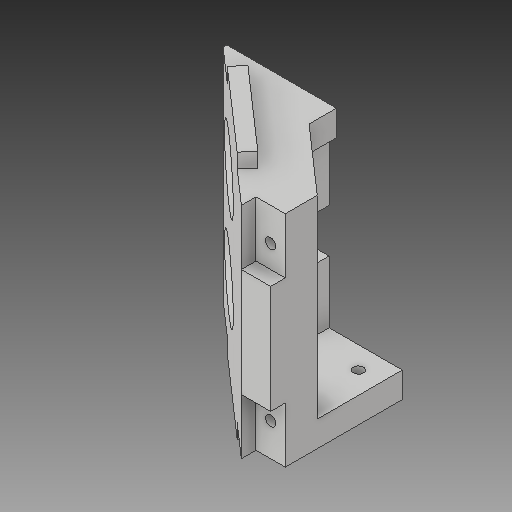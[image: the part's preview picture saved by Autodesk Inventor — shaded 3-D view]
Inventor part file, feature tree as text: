
AUTODESK INVENTOR PART (.ipt)
format: ipt  version: 2019 (Build 230136000, 136)  size: 202,752 bytes
history: native  units: mm
features: sketch x10, other x4, extrude x1, projected_geometry x1
ambient origin geometry x8: Origin, YZ Plane, XZ Plane, XY Plane, X Axis, Y Axis, Z Axis, Center Point
bodies: Body1 (feature_tree)
feature tree (16):
  other  "Sensor.ipt"
  extrude  "Выдавливание1"  Depth=10.0mm
  other  "Твердое тело1::Sensor.ipt"
  other  "Элемент создания тегов1"
  sketch  "Эскиз1"
  sketch  "Эскиз2"
  sketch  "Эскиз3"
  sketch  "Эскиз4"
  sketch  "Эскиз5"
  sketch  "Эскиз6"
  sketch  "Эскиз7"
  sketch  "Эскиз8"
  sketch  "Эскиз9"
  sketch  "Эскиз10"
  projected_geometry  "Спроецированная петля1"
  other  "Твердое тело1"
